# Revit family: Hager-Vega-IP40-sistema-NoHosted-CH-it
name_source: partatom
category: Electrical Equipment
units: mm (PartAtom-declared; Revit-internal decimal feet)

## family parameters
Always vertical = Yes
Cut with Voids When Loaded = No
Panel Configuration = Two Columns, Circuits Across
Part Type = Panelboard
Room Calculation Point = No
Round Connector Dimension = Use Diameter
Shared = No
Work Plane-Based = Yes

## types (8) — shared parameters
Default Elevation = 1219 mm
EF000003 - Tipo di montaggio = EV000384 - A parete
EF000007 - colore = EV000202 - bianco
EF000008 - Larghezza = 400 mm  [stored 1.31234 ft]
EF000049 - profondità = 146 mm  [stored 0.479003 ft]
EF000116 - numero RAL = 9010
EF000118 - con piastra di montaggio = No
EF000339 - tipo di copertura = EV004216 - porta
EF001062 - esecuzione EMC = No
EF001088 - possibilità di applicazione = Yes
EF001131 - profondità interna = 120 mm
EF001134 - barra DIN = Yes
EF001596 - Attacco Lampada = EV000139 - plastica
EF002950 - Numero moduli DIN = 18
EF004462 - tipo di chiusura = EV000154 - altri
EF005474 - grado di protezione (IP) = EV006415 - IP40
EF006306 - con serratura = No
EF009212 - esecuzione coperchio = EV000116 - chiuso
EF015776 - Morsettiera di terra = Yes
EF015777 - Morsettiera neutra = No
EF015941 - Segnale di passaggio porta = Yes
HG000001 - Numero di colonne = 1
HG000002 - Con porta = Yes
HG000003 - Gamma = Vega
HG000005 - Spessore = 3 mm  [stored 0.00984252 ft]
HG000006 - Ad incasso = No
HG000009 - Porta doppia a battente = No
HG000010 - Porte asimmetriche = No
HG000011 - File vuote nella parte basse = No
HG000017 - Distanza tra i poli = 18 mm  [stored 0.0590551 ft]
Manufacturer = Hager
Type Comments = Vega
zero-valued in all types: EF000218 - profondità di incasso, EF000332 - Altezza della parte incassata, EF000846 - larghezza di montaggio, HG000007 - Numero di colonne vuote, HG000008 - Numero di file vuote

## per-type parameters (varying)
| type | EF000040 - Altezza | EF000266 - numero di file | EF006244 - coperchio/porta trasparente | HG000004 - Codice produttore | Model |
| A parete IP40 L400 A325 P146 18 Unità di divisione - VB118B | 325 mm | 1 | No | VB118B | VB118B |
| A parete IP40 L400 A325 P146 18 Unità di divisione - VB118R | 325 mm | 1 | Yes | VB118R | VB118R |
| A parete IP40 L400 A475 P146 18 Unità di divisione - VB218B | 475 mm  [stored 1.5584 ft] | 2 | No | VB218B | VB218B |
| A parete IP40 L400 A475 P146 18 Unità di divisione - VB218R | 475 mm  [stored 1.5584 ft] | 2 | Yes | VB218R | VB218R |
| A parete IP40 L400 A625 P146 18 Unità di divisione - VB318B | 625 mm  [stored 2.05052 ft] | 3 | No | VB318B | VB318B |
| A parete IP40 L400 A625 P146 18 Unità di divisione - VB318R | 625 mm  [stored 2.05052 ft] | 3 | Yes | VB318R | VB318R |
| A parete IP40 L400 A775 P146 18 Unità di divisione - VB418B | 775 mm  [stored 2.54265 ft] | 4 | No | VB418B | VB418B |
| A parete IP40 L400 A775 P146 18 Unità di divisione - VB418R | 775 mm  [stored 2.54265 ft] | 4 | Yes | VB418R | VB418R |

note: [stored X ft] marks values corroborated as IEEE doubles in the binary element streams (Revit-internal decimal feet)

## geometry (parser evidence)
native form markers: Sweep x13
no freeform markers — native parametric forms only
